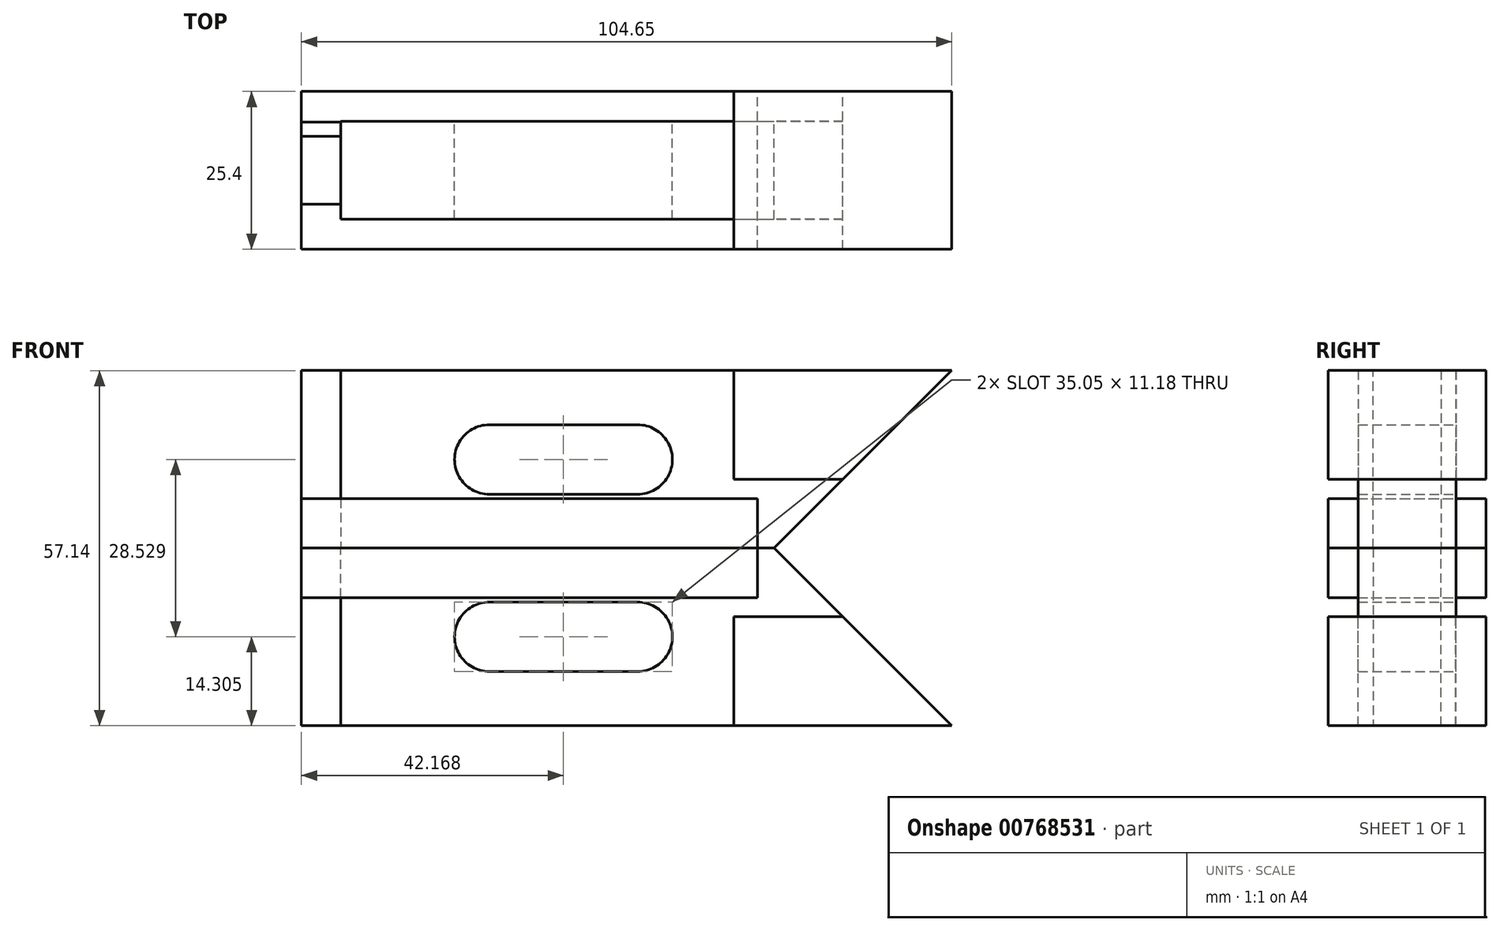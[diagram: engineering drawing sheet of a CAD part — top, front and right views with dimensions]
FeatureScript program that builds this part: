
annotation { "Feature Type Name" : "Feature", "Feature Type Description" : "" }
export const myFeature = defineFeature(function(context is Context, id is Id, definition is map)
    precondition{}
    {
        {
            var Q0;
            Q0=qCreatedBy(makeId("Front.planeOp"),FACE);
            var sketch = newSketch(context, id + "F0", { "sketchPlane" : qUnion([Q0])});
            skLineSegment(sketch, "E0.bottom", {"start": v(-13.6, 0) * mm, "end": v(91.04, 0) * mm});
            skLineSegment(sketch, "E0.top", {"start": v(-13.6, 28.57) * mm, "end": v(91.04, 28.57) * mm});
            skLineSegment(sketch, "E0.left", {"start": v(-13.6, 0) * mm, "end": v(-13.6, 28.57) * mm});
            skLineSegment(sketch, "E0.right", {"start": v(91.04, 0) * mm, "end": v(91.04, 28.57) * mm});
            skLineSegment(sketch, "E1", {"start": v(-13.6, 0) * mm, "end": v(-13.6, -7.95) * mm});
            skLineSegment(sketch, "E2", {"start": v(-13.6, -7.95) * mm, "end": v(59.8, -7.95) * mm});
            skLineSegment(sketch, "E3", {"start": v(59.8, -7.95) * mm, "end": v(59.8, 0) * mm});
            skLineSegment(sketch, "E4", {"start": v(91.04, 28.57) * mm, "end": v(62.47, 0) * mm});
            skLineSegment(sketch, "E5", {"start": v(-7.26, 28.57) * mm, "end": v(-7.26, 0) * mm});
            skLineSegment(sketch, "E6", {"start": v(56, 28.57) * mm, "end": v(56, 11.05) * mm});
            skLineSegment(sketch, "E7", {"start": v(56, 11.05) * mm, "end": v(73.52, 11.05) * mm});
            skArc(sketch, "E8", {"start": v(16.64, 19.85) * mm, "mid": v(11.03, 14.28) * mm, "end": v(16.62, 8.68) * mm});
            skLineSegment(sketch, "E9", {"start": v(16.6, 19.85) * mm, "end": v(40.48, 19.85) * mm});
            skLineSegment(sketch, "E10", {"start": v(40.48, 8.68) * mm, "end": v(40.48, 8.31) * mm});
            skLineSegment(sketch, "E11", {"start": v(16.62, 8.68) * mm, "end": v(40.48, 8.68) * mm});
            skArc(sketch, "E12", {"start": v(40.48, 8.68) * mm, "mid": v(46.08, 14.26) * mm, "end": v(40.48, 19.85) * mm});
            skPoint(sketch, "E12.third.point", {"position": v(35.77, 11.28) * mm});
            skSolve(sketch);
        }
        {
            var Q0;
            {var subQ0=sQuery(id+"F0.wireOp",EDGE,"E1");Q0=makeQuery(id+"F0.imprint","IMPRINT",FACE,{"disambiguationData":[TD([[makeQuery(id+"F0.imprint","IMPRINT",EDGE,{"derivedFrom":subQ0}),1.0]])]});}
            var Q1;
            {var subQ3=sQuery(id+"F0.wireOp",EDGE,"E6");Q1=makeQuery(id+"F0.imprint","IMPRINT",FACE,{"disambiguationData":[TD([[makeQuery(id+"F0.imprint","IMPRINT",EDGE,{"derivedFrom":subQ3}),1.0]])]});}
            extrude(context, id + "F1", {"entities" : qUnion([Q0, Q1]), "depth" : 25.4 * mm, "offsetDistance" : 25.4 * mm, "symmetric" : true});
        }
        {
            var Q0;
            {var subQ5=sQuery(id+"F0.wireOp",EDGE,"E5");Q0=makeQuery(id+"F0.imprint","IMPRINT",FACE,{"disambiguationData":[TD([[makeQuery(id+"F0.imprint","IMPRINT",EDGE,{"derivedFrom":subQ5}),1.0]])]});}
            extrude(context, id + "F2", {"entities" : qUnion([Q0]), "depth" : 15.75 * mm, "offsetDistance" : 25.4 * mm, "symmetric" : true});
        }
        {
            var Q0;
            {var subQ0=sQuery(id+"F0.wireOp",EDGE,"E0.left");Q0=makeQuery(id+"F0.imprint","IMPRINT",FACE,{"disambiguationData":[TD([[makeQuery(id+"F0.imprint","IMPRINT",EDGE,{"derivedFrom":subQ0}),-1.0]])]});}
            extrude(context, id + "F3", {"entities" : qUnion([Q0]), "depth" : 10.92 * mm, "offsetDistance" : 25.4 * mm, "symmetric" : true});
        }
        {
            var Q0;
            Q0=makeQuery(id+"F3.opExtrude","CAP_FACE",FACE,{"disambiguationData":[OSD([sQuery(id+"F0.wireOp",EDGE,"E0.bottom"),sQuery(id+"F0.wireOp",EDGE,"E0.top"),sQuery(id+"F0.wireOp",EDGE,"E0.left"),sQuery(id+"F0.wireOp",EDGE,"E5")])],"isStart":true});
            extrude(context, id + "F4", {"entities" : qUnion([Q0]), "depth" : 2.34 * mm, "offsetDistance" : 25.4 * mm});
        }
        {
            var Q0;
            Q0=makeQuery(id+"F1.opExtrude","SWEPT_BODY",BODY,{"disambiguationData":[OSD([sQuery(id+"F0.wireOp",EDGE,"E0.top"),sQuery(id+"F0.wireOp",EDGE,"E4"),sQuery(id+"F0.wireOp",EDGE,"E6"),sQuery(id+"F0.wireOp",EDGE,"E7")])]});
            var Q1;
            Q1=makeQuery(id+"F1.opExtrude","SWEPT_BODY",BODY,{"disambiguationData":[OSD([sQuery(id+"F0.wireOp",EDGE,"E0.bottom"),sQuery(id+"F0.wireOp",EDGE,"E1"),sQuery(id+"F0.wireOp",EDGE,"E2"),sQuery(id+"F0.wireOp",EDGE,"E3")])]});
            var Q2;
            Q2=makeQuery(id+"F2.opExtrude","SWEPT_BODY",BODY,{"disambiguationData":[OSD([sQuery(id+"F0.wireOp",EDGE,"E0.bottom"),sQuery(id+"F0.wireOp",EDGE,"E0.top"),sQuery(id+"F0.wireOp",EDGE,"E4"),sQuery(id+"F0.wireOp",EDGE,"E5"),sQuery(id+"F0.wireOp",EDGE,"E6"),sQuery(id+"F0.wireOp",EDGE,"E7"),sQuery(id+"F0.wireOp",EDGE,"E8"),sQuery(id+"F0.wireOp",EDGE,"E9"),sQuery(id+"F0.wireOp",EDGE,"E11"),sQuery(id+"F0.wireOp",EDGE,"E12")])]});
            var Q3;
            Q3=makeQuery(id+"F3.opExtrude","SWEPT_BODY",BODY,{"disambiguationData":[OSD([sQuery(id+"F0.wireOp",EDGE,"E0.bottom"),sQuery(id+"F0.wireOp",EDGE,"E0.top"),sQuery(id+"F0.wireOp",EDGE,"E0.left"),sQuery(id+"F0.wireOp",EDGE,"E5")])]});
            var Q4;
            Q4=makeQuery(id+"F4.opExtrude","SWEPT_BODY",BODY,{"disambiguationData":[OSD([sQuery(id+"F0.wireOp",EDGE,"E0.bottom"),sQuery(id+"F0.wireOp",EDGE,"E0.top"),sQuery(id+"F0.wireOp",EDGE,"E0.left"),sQuery(id+"F0.wireOp",EDGE,"E5")])]});
            var Q5;
            Q5=qCreatedBy(makeId("Top.planeOp"),FACE);
            mirror(context, id + "F5", {"entities" : qUnion([Q0, Q1, Q2, Q3, Q4]), "mirrorPlane" : qUnion([Q5])});
        }
    });
